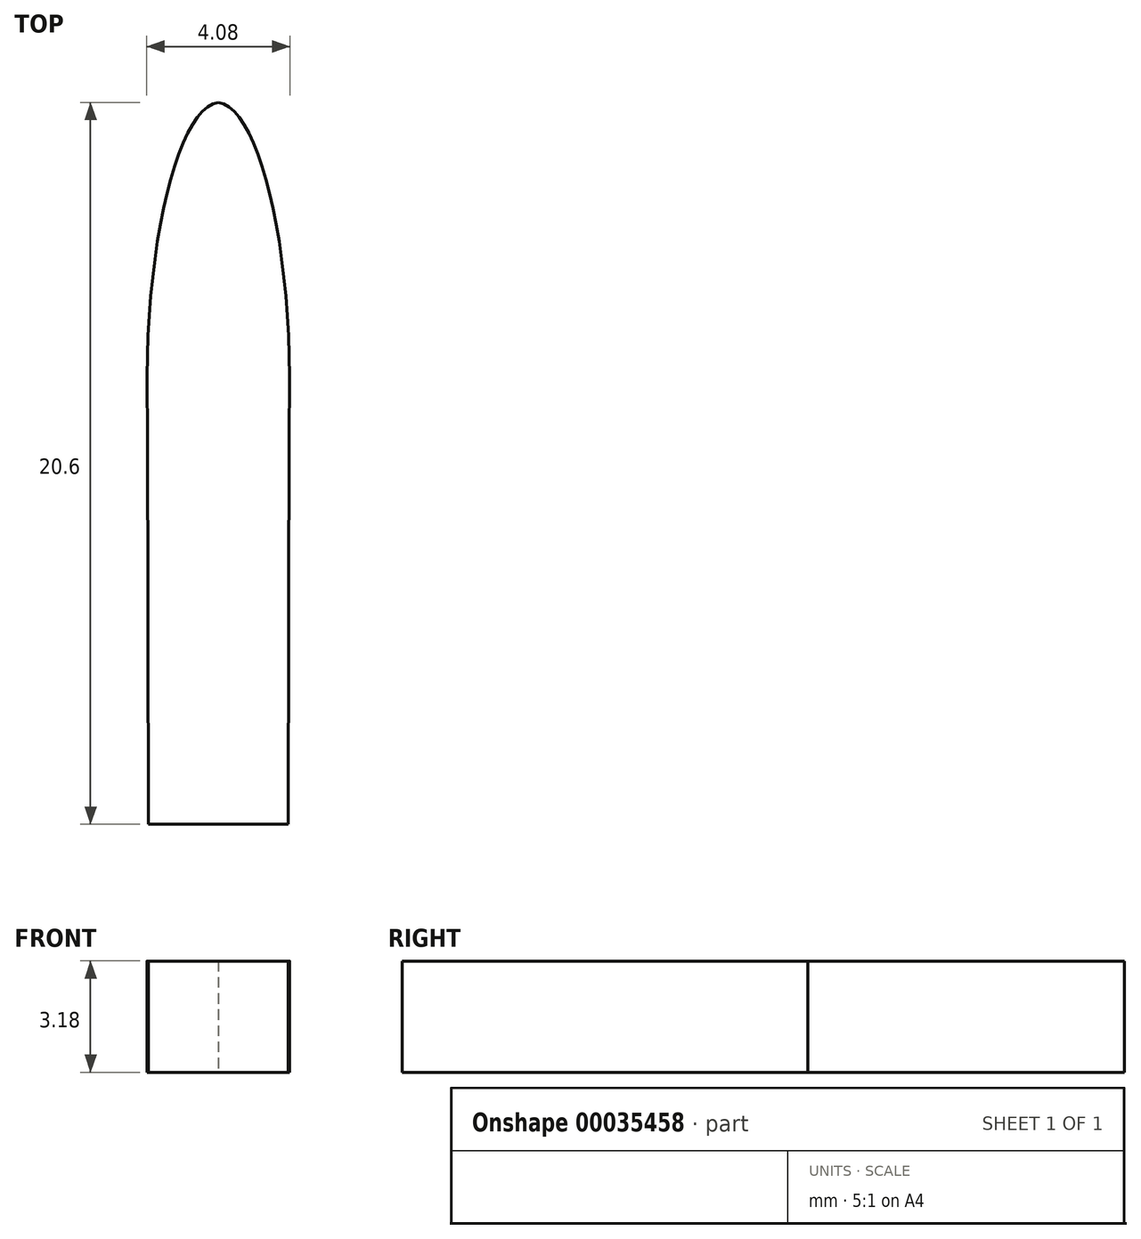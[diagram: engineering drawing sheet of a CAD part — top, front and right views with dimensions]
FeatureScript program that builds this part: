
annotation { "Feature Type Name" : "Feature", "Feature Type Description" : "" }
export const myFeature = defineFeature(function(context is Context, id is Id, definition is map)
    precondition{}
    {
        {
            var Q0;
            Q0=qCreatedBy(makeId("Top.planeOp"),FACE);
            var sketch = newSketch(context, id + "F0", { "sketchPlane" : qUnion([Q0])});
            skLineSegment(sketch, "E0", {"start": v(-2, -11.57) * mm, "end": v(0, -11.57) * mm});
            skFitSpline(sketch, "E1", {"points": [v(2.68, 0) * mm, v(0, 9.03) * mm, v(-2.02, 0) * mm], "startDerivative": vector(-0.52, 30.69) * mm, "endDerivative": vector(0.95, -28.23) * mm});
            skLineSegment(sketch, "E2", {"start": v(-2.02, 0) * mm, "end": v(-2, -11.57) * mm});
            skFitSpline(sketch, "E3.MirrorCS", {"points": [v(-2.68, 0) * mm, v(0, 9.03) * mm, v(2.02, 0) * mm], "startDerivative": vector(0.52, 30.69) * mm, "endDerivative": vector(-0.95, -28.23) * mm});
            skLineSegment(sketch, "E4.MirrorCS", {"start": v(2.02, 0) * mm, "end": v(2, -11.57) * mm});
            skLineSegment(sketch, "E5.MirrorCS", {"start": v(2, -11.57) * mm, "end": v(0, -11.57) * mm});
            skSolve(sketch);
        }
        {
            var Q0;
            Q0=makeQuery(id+"F0.imprint","IMPRINT",FACE,{"disambiguationData":[TD([[makeQuery(id+"F0.imprint","IMPRINT",EDGE,{"derivedFrom":sQuery(id+"F0.wireOp",EDGE,"E0")}),1.0]])]});
            extrude(context, id + "F1", {"entities" : qUnion([Q0]), "depth" : 3.17 * mm});
        }
    });
